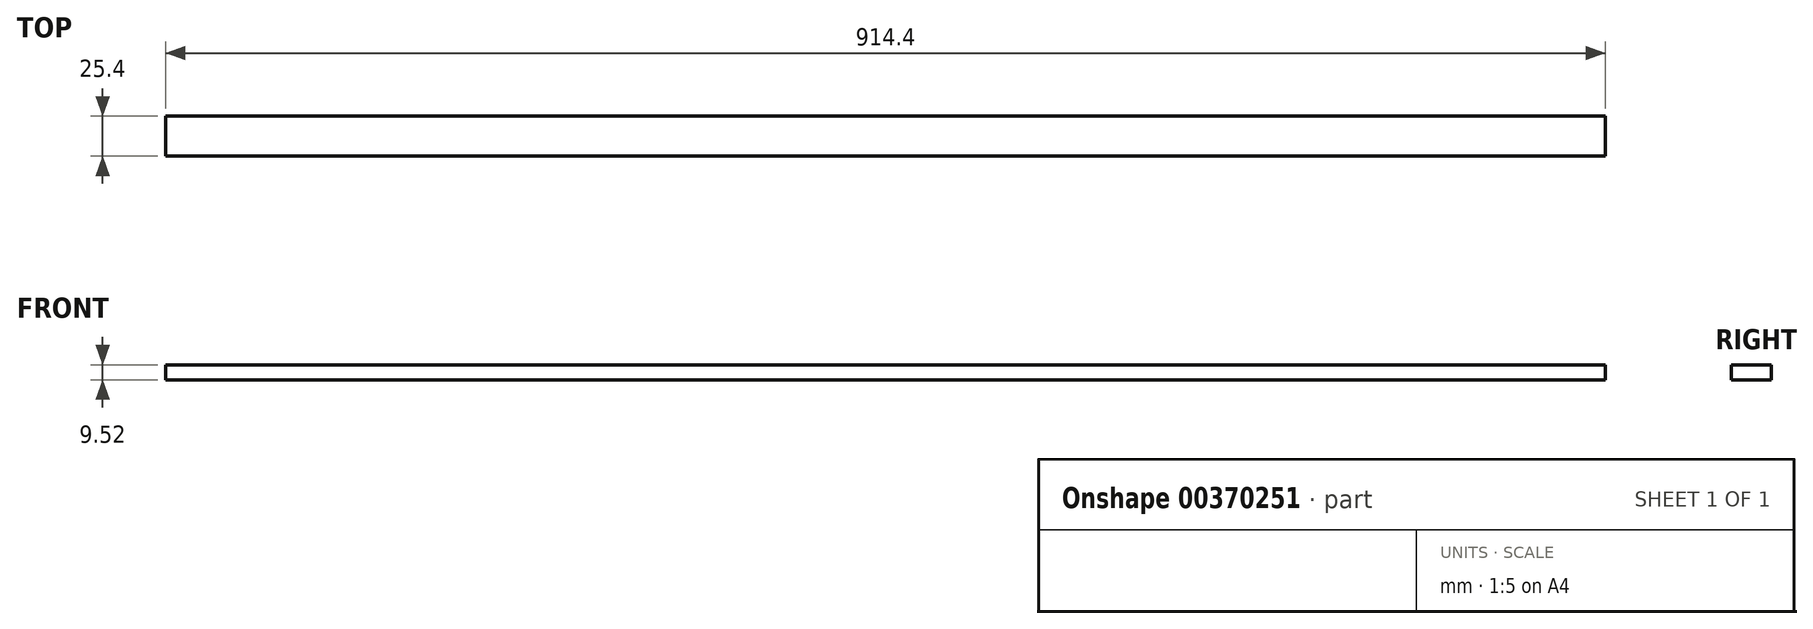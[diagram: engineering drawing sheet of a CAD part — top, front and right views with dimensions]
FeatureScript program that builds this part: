
annotation { "Feature Type Name" : "Feature", "Feature Type Description" : "" }
export const myFeature = defineFeature(function(context is Context, id is Id, definition is map)
    precondition{}
    {
        {
            var Q0;
            Q0=qCreatedBy(makeId("Top.planeOp"),FACE);
            var sketch = newSketch(context, id + "F0", { "sketchPlane" : qUnion([Q0])});
            skLineSegment(sketch, "E0.bottom", {"start": v(-457.2, -12.7) * mm, "end": v(457.2, -12.7) * mm});
            skLineSegment(sketch, "E0.top", {"start": v(-457.2, 12.7) * mm, "end": v(457.2, 12.7) * mm});
            skLineSegment(sketch, "E0.left", {"start": v(-457.2, -12.7) * mm, "end": v(-457.2, 12.7) * mm});
            skLineSegment(sketch, "E0.right", {"start": v(457.2, -12.7) * mm, "end": v(457.2, 12.7) * mm});
            skPoint(sketch, "E0.middle", {"position": v(0, 0) * mm});
            skSolve(sketch);
        }
        {
            var Q0;
            Q0=makeQuery(id+"F0.imprint","IMPRINT",FACE,{"disambiguationData":[TD([[makeQuery(id+"F0.imprint","IMPRINT",EDGE,{"derivedFrom":sQuery(id+"F0.wireOp",EDGE,"E0.bottom")}),1.0]])]});
            extrude(context, id + "F1", {"entities" : qUnion([Q0]), "endBound" : BoundingType.SYMMETRIC, "oppositeDirection" : true, "depth" : 9.52 * mm});
        }
    });
